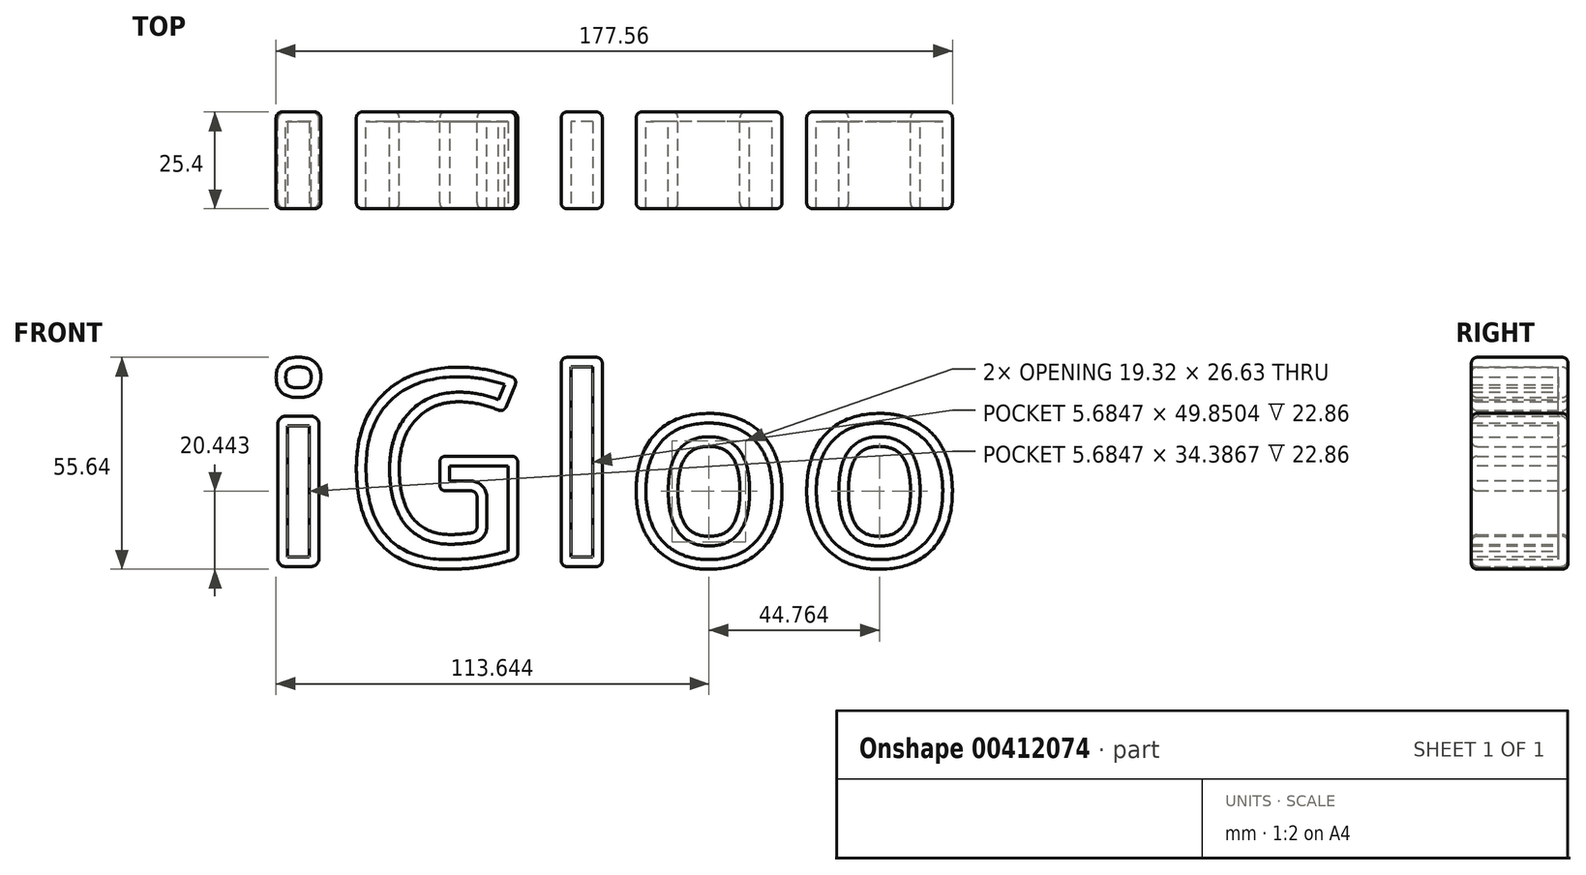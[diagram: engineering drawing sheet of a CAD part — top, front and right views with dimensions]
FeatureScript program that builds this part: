
annotation { "Feature Type Name" : "Feature", "Feature Type Description" : "" }
export const myFeature = defineFeature(function(context is Context, id is Id, definition is map)
    precondition{}
    {
        {
            var Q0;
            Q0=qCreatedBy(makeId("Front.planeOp"),FACE);
            var sketch = newSketch(context, id + "F0", { "sketchPlane" : qUnion([Q0])});
            skText(sketch, "E0", { "text": "iGloo", "fontName": "OpenSans-Bold.ttf"});
            const initialGuessF0  = {"E0": [-0.10189, -0.01132, 1, 0, 0.05205]};
            skSetInitialGuess(sketch, initialGuessF0);
            skSolve(sketch);
        }
        {
            var Q0;
            Q0 = qSketchRegion(id + "F0", true);
            var Q1;
            Q1 = qConstructionFilter(qBodyType(qCreatedBy(id + "F0" ,EDGE), BodyType.WIRE), ConstructionObject.NO);
            extrude(context, id + "F1", {"entities" : qUnion([Q0]), "surfaceEntities" : qUnion([Q1]), "depth" : 25.4 * mm});
        }
        {
            assignVariable(context, id + "F2", {"name" : "FilletAmount", "anyValue" : 1.52 * mm});
        }
        {
            var Q0;
            Q0=makeQuery(id+"F1.opExtrude","CAP_EDGE",EDGE,{"disambiguationData":[OSD([sQuery(id+"F0.wireOp",EDGE,"E0.sketch_text.stroke-7")])],"isStart":false});
            var Q1;
            Q1=makeQuery(id+"F1.opExtrude","CAP_EDGE",EDGE,{"disambiguationData":[OSD([sQuery(id+"F0.wireOp",EDGE,"E0.sketch_text.stroke-8")])],"isStart":false});
            var Q2;
            Q2=makeQuery(id+"F1.opExtrude","CAP_EDGE",EDGE,{"disambiguationData":[OSD([sQuery(id+"F0.wireOp",EDGE,"E0.sketch_text.stroke-6")])],"isStart":false});
            var Q3;
            Q3=makeQuery(id+"F1.opExtrude","CAP_EDGE",EDGE,{"disambiguationData":[OSD([sQuery(id+"F0.wireOp",EDGE,"E0.sketch_text.stroke-5")])],"isStart":false});
            var Q4;
            Q4=makeQuery(id+"F1.opExtrude","SWEPT_EDGE",EDGE,{"disambiguationData":[OSD([sQuery(id+"F0.wireOp",EDGE,"E0.sketch_text.stroke-7"),sQuery(id+"F0.wireOp",EDGE,"E0.sketch_text.stroke-8")])]});
            var Q5;
            Q5=makeQuery(id+"F1.opExtrude","CAP_EDGE",EDGE,{"disambiguationData":[OSD([sQuery(id+"F0.wireOp",EDGE,"E0.sketch_text.stroke-5")])],"isStart":true});
            var Q6;
            Q6=makeQuery(id+"F1.opExtrude","CAP_EDGE",EDGE,{"disambiguationData":[OSD([sQuery(id+"F0.wireOp",EDGE,"E0.sketch_text.stroke-7")])],"isStart":true});
            var Q7;
            Q7=makeQuery(id+"F1.opExtrude","SWEPT_EDGE",EDGE,{"disambiguationData":[OSD([sQuery(id+"F0.wireOp",EDGE,"E0.sketch_text.stroke-5"),sQuery(id+"F0.wireOp",EDGE,"E0.sketch_text.stroke-6")])]});
            var Q8;
            Q8=makeQuery(id+"F1.opExtrude","SWEPT_EDGE",EDGE,{"disambiguationData":[OSD([sQuery(id+"F0.wireOp",EDGE,"E0.sketch_text.stroke-6"),sQuery(id+"F0.wireOp",EDGE,"E0.sketch_text.stroke-7")])]});
            var Q9;
            Q9=makeQuery(id+"F1.opExtrude","SWEPT_EDGE",EDGE,{"disambiguationData":[OSD([sQuery(id+"F0.wireOp",EDGE,"E0.sketch_text.stroke-5"),sQuery(id+"F0.wireOp",EDGE,"E0.sketch_text.stroke-8")])]});
            var Q10;
            Q10=makeQuery(id+"F1.opExtrude","CAP_EDGE",EDGE,{"disambiguationData":[OSD([sQuery(id+"F0.wireOp",EDGE,"E0.sketch_text.stroke-6")])],"isStart":true});
            var Q11;
            Q11=makeQuery(id+"F1.opExtrude","CAP_EDGE",EDGE,{"disambiguationData":[OSD([sQuery(id+"F0.wireOp",EDGE,"E0.sketch_text.stroke-8")])],"isStart":true});
            fillet(context, id + "F3", {"entities" : qUnion([Q0, Q1, Q2, Q3, Q4, Q5, Q6, Q7, Q8, Q9, Q10, Q11]), "radius" : 2.03 * mm, "tangentPropagation" : true, "allowEdgeOverflow" : false});
        }
        {
            var Q0;
            Q0=makeQuery(id+"F1.opExtrude","SWEPT_FACE",FACE,{"disambiguationData":[OSD([sQuery(id+"F0.wireOp",EDGE,"E0.sketch_text.stroke-0")])]});
            var Q1;
            Q1=makeQuery(id+"F1.opExtrude","CAP_FACE",FACE,{"disambiguationData":[OSD([sQuery(id+"F0.wireOp",EDGE,"E0.sketch_text.stroke-0"),sQuery(id+"F0.wireOp",EDGE,"E0.sketch_text.stroke-1"),sQuery(id+"F0.wireOp",EDGE,"E0.sketch_text.stroke-2"),sQuery(id+"F0.wireOp",EDGE,"E0.sketch_text.stroke-3"),sQuery(id+"F0.wireOp",EDGE,"E0.sketch_text.stroke-4")])],"isStart":false});
            var Q2;
            Q2=makeQuery(id+"F1.opExtrude","SWEPT_FACE",FACE,{"disambiguationData":[OSD([sQuery(id+"F0.wireOp",EDGE,"E0.sketch_text.stroke-1")])]});
            var Q3;
            Q3=makeQuery(id+"F1.opExtrude","SWEPT_FACE",FACE,{"disambiguationData":[OSD([sQuery(id+"F0.wireOp",EDGE,"E0.sketch_text.stroke-2")])]});
            var Q4;
            Q4=makeQuery(id+"F1.opExtrude","SWEPT_FACE",FACE,{"disambiguationData":[OSD([sQuery(id+"F0.wireOp",EDGE,"E0.sketch_text.stroke-3")])]});
            var Q5;
            Q5=makeQuery(id+"F1.opExtrude","SWEPT_FACE",FACE,{"disambiguationData":[OSD([sQuery(id+"F0.wireOp",EDGE,"E0.sketch_text.stroke-4")])]});
            var Q6;
            Q6=makeQuery(id+"F1.opExtrude","CAP_EDGE",EDGE,{"disambiguationData":[OSD([sQuery(id+"F0.wireOp",EDGE,"E0.sketch_text.stroke-0")])],"isStart":false});
            var Q7;
            Q7=makeQuery(id+"F1.opExtrude","CAP_EDGE",EDGE,{"disambiguationData":[OSD([sQuery(id+"F0.wireOp",EDGE,"E0.sketch_text.stroke-1")])],"isStart":false});
            var Q8;
            Q8=makeQuery(id+"F1.opExtrude","SWEPT_EDGE",EDGE,{"disambiguationData":[OSD([sQuery(id+"F0.wireOp",EDGE,"E0.sketch_text.stroke-0"),sQuery(id+"F0.wireOp",EDGE,"E0.sketch_text.stroke-4")])]});
            var Q9;
            Q9=makeQuery(id+"F1.opExtrude","SWEPT_EDGE",EDGE,{"disambiguationData":[OSD([sQuery(id+"F0.wireOp",EDGE,"E0.sketch_text.stroke-0"),sQuery(id+"F0.wireOp",EDGE,"E0.sketch_text.stroke-1")])]});
            var Q10;
            Q10=makeQuery(id+"F1.opExtrude","CAP_FACE",FACE,{"disambiguationData":[OSD([sQuery(id+"F0.wireOp",EDGE,"E0.sketch_text.stroke-0"),sQuery(id+"F0.wireOp",EDGE,"E0.sketch_text.stroke-1"),sQuery(id+"F0.wireOp",EDGE,"E0.sketch_text.stroke-2"),sQuery(id+"F0.wireOp",EDGE,"E0.sketch_text.stroke-3"),sQuery(id+"F0.wireOp",EDGE,"E0.sketch_text.stroke-4")])],"isStart":true});
            var Q11;
            Q11=makeQuery(id+"F1.opExtrude","SWEPT_EDGE",EDGE,{"disambiguationData":[OSD([sQuery(id+"F0.wireOp",EDGE,"E0.sketch_text.stroke-1"),sQuery(id+"F0.wireOp",EDGE,"E0.sketch_text.stroke-2")])]});
            var Q12;
            Q12=makeQuery(id+"F1.opExtrude","SWEPT_EDGE",EDGE,{"disambiguationData":[OSD([sQuery(id+"F0.wireOp",EDGE,"E0.sketch_text.stroke-2"),sQuery(id+"F0.wireOp",EDGE,"E0.sketch_text.stroke-3")])]});
            var Q13;
            Q13=makeQuery(id+"F1.opExtrude","SWEPT_EDGE",EDGE,{"disambiguationData":[OSD([sQuery(id+"F0.wireOp",EDGE,"E0.sketch_text.stroke-3"),sQuery(id+"F0.wireOp",EDGE,"E0.sketch_text.stroke-4")])]});
            var Q14;
            Q14=makeQuery(id+"F1.opExtrude","CAP_EDGE",EDGE,{"disambiguationData":[OSD([sQuery(id+"F0.wireOp",EDGE,"E0.sketch_text.stroke-4")])],"isStart":false});
            var Q15;
            Q15=makeQuery(id+"F1.opExtrude","CAP_EDGE",EDGE,{"disambiguationData":[OSD([sQuery(id+"F0.wireOp",EDGE,"E0.sketch_text.stroke-0")])],"isStart":true});
            var Q16;
            Q16=makeQuery(id+"F1.opExtrude","CAP_EDGE",EDGE,{"disambiguationData":[OSD([sQuery(id+"F0.wireOp",EDGE,"E0.sketch_text.stroke-1")])],"isStart":true});
            var Q17;
            Q17=makeQuery(id+"F1.opExtrude","CAP_EDGE",EDGE,{"disambiguationData":[OSD([sQuery(id+"F0.wireOp",EDGE,"E0.sketch_text.stroke-2")])],"isStart":false});
            var Q18;
            Q18=makeQuery(id+"F1.opExtrude","CAP_EDGE",EDGE,{"disambiguationData":[OSD([sQuery(id+"F0.wireOp",EDGE,"E0.sketch_text.stroke-3")])],"isStart":false});
            var Q19;
            Q19=makeQuery(id+"F1.opExtrude","CAP_EDGE",EDGE,{"disambiguationData":[OSD([sQuery(id+"F0.wireOp",EDGE,"E0.sketch_text.stroke-2")])],"isStart":true});
            var Q20;
            Q20=makeQuery(id+"F1.opExtrude","CAP_EDGE",EDGE,{"disambiguationData":[OSD([sQuery(id+"F0.wireOp",EDGE,"E0.sketch_text.stroke-3")])],"isStart":true});
            var Q21;
            Q21=makeQuery(id+"F1.opExtrude","CAP_EDGE",EDGE,{"disambiguationData":[OSD([sQuery(id+"F0.wireOp",EDGE,"E0.sketch_text.stroke-4")])],"isStart":true});
            fillet(context, id + "F4", {"entities" : qUnion([Q0, Q1, Q2, Q3, Q4, Q5, Q6, Q7, Q8, Q9, Q10, Q11, Q12, Q13, Q14, Q15, Q16, Q17, Q18, Q19, Q20, Q21]), "radius" : getVariable(context, 'FilletAmount'), "tangentPropagation" : true, "allowEdgeOverflow" : false});
        }
        {
            var Q0;
            Q0=makeQuery(id+"F1.opExtrude","CAP_FACE",FACE,{"disambiguationData":[OSD([sQuery(id+"F0.wireOp",EDGE,"E0.sketch_text.stroke-9"),sQuery(id+"F0.wireOp",EDGE,"E0.sketch_text.stroke-10"),sQuery(id+"F0.wireOp",EDGE,"E0.sketch_text.stroke-11"),sQuery(id+"F0.wireOp",EDGE,"E0.sketch_text.stroke-12"),sQuery(id+"F0.wireOp",EDGE,"E0.sketch_text.stroke-13"),sQuery(id+"F0.wireOp",EDGE,"E0.sketch_text.stroke-14"),sQuery(id+"F0.wireOp",EDGE,"E0.sketch_text.stroke-15"),sQuery(id+"F0.wireOp",EDGE,"E0.sketch_text.stroke-16"),sQuery(id+"F0.wireOp",EDGE,"E0.sketch_text.stroke-17"),sQuery(id+"F0.wireOp",EDGE,"E0.sketch_text.stroke-18"),sQuery(id+"F0.wireOp",EDGE,"E0.sketch_text.stroke-19"),sQuery(id+"F0.wireOp",EDGE,"E0.sketch_text.stroke-20"),sQuery(id+"F0.wireOp",EDGE,"E0.sketch_text.stroke-21"),sQuery(id+"F0.wireOp",EDGE,"E0.sketch_text.stroke-22"),sQuery(id+"F0.wireOp",EDGE,"E0.sketch_text.stroke-23"),sQuery(id+"F0.wireOp",EDGE,"E0.sketch_text.stroke-24"),sQuery(id+"F0.wireOp",EDGE,"E0.sketch_text.stroke-25"),sQuery(id+"F0.wireOp",EDGE,"E0.sketch_text.stroke-26"),sQuery(id+"F0.wireOp",EDGE,"E0.sketch_text.stroke-27")])],"isStart":false});
            var Q1;
            Q1=makeQuery(id+"F1.opExtrude","SWEPT_FACE",FACE,{"disambiguationData":[OSD([sQuery(id+"F0.wireOp",EDGE,"E0.sketch_text.stroke-9")])]});
            var Q2;
            Q2=makeQuery(id+"F1.opExtrude","SWEPT_FACE",FACE,{"disambiguationData":[OSD([sQuery(id+"F0.wireOp",EDGE,"E0.sketch_text.stroke-25")])]});
            var Q3;
            Q3=makeQuery(id+"F1.opExtrude","CAP_EDGE",EDGE,{"disambiguationData":[OSD([sQuery(id+"F0.wireOp",EDGE,"E0.sketch_text.stroke-12")])],"isStart":false});
            var Q4;
            Q4=makeQuery(id+"F1.opExtrude","CAP_EDGE",EDGE,{"disambiguationData":[OSD([sQuery(id+"F0.wireOp",EDGE,"E0.sketch_text.stroke-20")])],"isStart":false});
            var Q5;
            Q5=makeQuery(id+"F1.opExtrude","SWEPT_FACE",FACE,{"disambiguationData":[OSD([sQuery(id+"F0.wireOp",EDGE,"E0.sketch_text.stroke-23")])]});
            var Q6;
            Q6=makeQuery(id+"F1.opExtrude","SWEPT_FACE",FACE,{"disambiguationData":[OSD([sQuery(id+"F0.wireOp",EDGE,"E0.sketch_text.stroke-24")])]});
            var Q7;
            Q7=makeQuery(id+"F1.opExtrude","CAP_EDGE",EDGE,{"disambiguationData":[OSD([sQuery(id+"F0.wireOp",EDGE,"E0.sketch_text.stroke-13")])],"isStart":false});
            var Q8;
            Q8=makeQuery(id+"F1.opExtrude","CAP_EDGE",EDGE,{"disambiguationData":[OSD([sQuery(id+"F0.wireOp",EDGE,"E0.sketch_text.stroke-21")])],"isStart":false});
            var Q9;
            Q9=makeQuery(id+"F1.opExtrude","SWEPT_FACE",FACE,{"disambiguationData":[OSD([sQuery(id+"F0.wireOp",EDGE,"E0.sketch_text.stroke-10")])]});
            var Q10;
            Q10=makeQuery(id+"F1.opExtrude","SWEPT_FACE",FACE,{"disambiguationData":[OSD([sQuery(id+"F0.wireOp",EDGE,"E0.sketch_text.stroke-26")])]});
            var Q11;
            Q11=makeQuery(id+"F1.opExtrude","CAP_EDGE",EDGE,{"disambiguationData":[OSD([sQuery(id+"F0.wireOp",EDGE,"E0.sketch_text.stroke-14")])],"isStart":false});
            var Q12;
            Q12=makeQuery(id+"F1.opExtrude","CAP_EDGE",EDGE,{"disambiguationData":[OSD([sQuery(id+"F0.wireOp",EDGE,"E0.sketch_text.stroke-22")])],"isStart":false});
            var Q13;
            Q13=makeQuery(id+"F1.opExtrude","CAP_EDGE",EDGE,{"disambiguationData":[OSD([sQuery(id+"F0.wireOp",EDGE,"E0.sketch_text.stroke-15")])],"isStart":false});
            var Q14;
            Q14=makeQuery(id+"F1.opExtrude","CAP_EDGE",EDGE,{"disambiguationData":[OSD([sQuery(id+"F0.wireOp",EDGE,"E0.sketch_text.stroke-23")])],"isStart":false});
            var Q15;
            Q15=makeQuery(id+"F1.opExtrude","SWEPT_FACE",FACE,{"disambiguationData":[OSD([sQuery(id+"F0.wireOp",EDGE,"E0.sketch_text.stroke-13")])]});
            var Q16;
            Q16=makeQuery(id+"F1.opExtrude","SWEPT_FACE",FACE,{"disambiguationData":[OSD([sQuery(id+"F0.wireOp",EDGE,"E0.sketch_text.stroke-14")])]});
            var Q17;
            Q17=makeQuery(id+"F1.opExtrude","CAP_EDGE",EDGE,{"disambiguationData":[OSD([sQuery(id+"F0.wireOp",EDGE,"E0.sketch_text.stroke-16")])],"isStart":false});
            var Q18;
            Q18=makeQuery(id+"F1.opExtrude","CAP_EDGE",EDGE,{"disambiguationData":[OSD([sQuery(id+"F0.wireOp",EDGE,"E0.sketch_text.stroke-24")])],"isStart":false});
            var Q19;
            Q19=makeQuery(id+"F1.opExtrude","SWEPT_FACE",FACE,{"disambiguationData":[OSD([sQuery(id+"F0.wireOp",EDGE,"E0.sketch_text.stroke-15")])]});
            var Q20;
            Q20=makeQuery(id+"F1.opExtrude","SWEPT_FACE",FACE,{"disambiguationData":[OSD([sQuery(id+"F0.wireOp",EDGE,"E0.sketch_text.stroke-16")])]});
            var Q21;
            Q21=makeQuery(id+"F1.opExtrude","CAP_EDGE",EDGE,{"disambiguationData":[OSD([sQuery(id+"F0.wireOp",EDGE,"E0.sketch_text.stroke-17")])],"isStart":false});
            var Q22;
            Q22=makeQuery(id+"F1.opExtrude","SWEPT_FACE",FACE,{"disambiguationData":[OSD([sQuery(id+"F0.wireOp",EDGE,"E0.sketch_text.stroke-17")])]});
            var Q23;
            Q23=makeQuery(id+"F1.opExtrude","CAP_EDGE",EDGE,{"disambiguationData":[OSD([sQuery(id+"F0.wireOp",EDGE,"E0.sketch_text.stroke-18")])],"isStart":false});
            var Q24;
            Q24=makeQuery(id+"F1.opExtrude","SWEPT_FACE",FACE,{"disambiguationData":[OSD([sQuery(id+"F0.wireOp",EDGE,"E0.sketch_text.stroke-19")])]});
            var Q25;
            Q25=makeQuery(id+"F1.opExtrude","SWEPT_FACE",FACE,{"disambiguationData":[OSD([sQuery(id+"F0.wireOp",EDGE,"E0.sketch_text.stroke-20")])]});
            var Q26;
            Q26=makeQuery(id+"F1.opExtrude","CAP_EDGE",EDGE,{"disambiguationData":[OSD([sQuery(id+"F0.wireOp",EDGE,"E0.sketch_text.stroke-11")])],"isStart":false});
            var Q27;
            Q27=makeQuery(id+"F1.opExtrude","CAP_EDGE",EDGE,{"disambiguationData":[OSD([sQuery(id+"F0.wireOp",EDGE,"E0.sketch_text.stroke-19")])],"isStart":false});
            var Q28;
            Q28=makeQuery(id+"F1.opExtrude","SWEPT_FACE",FACE,{"disambiguationData":[OSD([sQuery(id+"F0.wireOp",EDGE,"E0.sketch_text.stroke-21")])]});
            var Q29;
            Q29=makeQuery(id+"F1.opExtrude","SWEPT_FACE",FACE,{"disambiguationData":[OSD([sQuery(id+"F0.wireOp",EDGE,"E0.sketch_text.stroke-22")])]});
            var Q30;
            Q30=makeQuery(id+"F1.opExtrude","SWEPT_EDGE",EDGE,{"disambiguationData":[OSD([sQuery(id+"F0.wireOp",EDGE,"E0.sketch_text.stroke-13"),sQuery(id+"F0.wireOp",EDGE,"E0.sketch_text.stroke-14")])]});
            var Q31;
            Q31=makeQuery(id+"F1.opExtrude","CAP_FACE",FACE,{"disambiguationData":[OSD([sQuery(id+"F0.wireOp",EDGE,"E0.sketch_text.stroke-9"),sQuery(id+"F0.wireOp",EDGE,"E0.sketch_text.stroke-10"),sQuery(id+"F0.wireOp",EDGE,"E0.sketch_text.stroke-11"),sQuery(id+"F0.wireOp",EDGE,"E0.sketch_text.stroke-12"),sQuery(id+"F0.wireOp",EDGE,"E0.sketch_text.stroke-13"),sQuery(id+"F0.wireOp",EDGE,"E0.sketch_text.stroke-14"),sQuery(id+"F0.wireOp",EDGE,"E0.sketch_text.stroke-15"),sQuery(id+"F0.wireOp",EDGE,"E0.sketch_text.stroke-16"),sQuery(id+"F0.wireOp",EDGE,"E0.sketch_text.stroke-17"),sQuery(id+"F0.wireOp",EDGE,"E0.sketch_text.stroke-18"),sQuery(id+"F0.wireOp",EDGE,"E0.sketch_text.stroke-19"),sQuery(id+"F0.wireOp",EDGE,"E0.sketch_text.stroke-20"),sQuery(id+"F0.wireOp",EDGE,"E0.sketch_text.stroke-21"),sQuery(id+"F0.wireOp",EDGE,"E0.sketch_text.stroke-22"),sQuery(id+"F0.wireOp",EDGE,"E0.sketch_text.stroke-23"),sQuery(id+"F0.wireOp",EDGE,"E0.sketch_text.stroke-24"),sQuery(id+"F0.wireOp",EDGE,"E0.sketch_text.stroke-25"),sQuery(id+"F0.wireOp",EDGE,"E0.sketch_text.stroke-26"),sQuery(id+"F0.wireOp",EDGE,"E0.sketch_text.stroke-27")])],"isStart":true});
            var Q32;
            Q32=makeQuery(id+"F1.opExtrude","SWEPT_EDGE",EDGE,{"disambiguationData":[OSD([sQuery(id+"F0.wireOp",EDGE,"E0.sketch_text.stroke-14"),sQuery(id+"F0.wireOp",EDGE,"E0.sketch_text.stroke-15")])]});
            var Q33;
            Q33=makeQuery(id+"F1.opExtrude","SWEPT_EDGE",EDGE,{"disambiguationData":[OSD([sQuery(id+"F0.wireOp",EDGE,"E0.sketch_text.stroke-9"),sQuery(id+"F0.wireOp",EDGE,"E0.sketch_text.stroke-10")])]});
            var Q34;
            Q34=makeQuery(id+"F1.opExtrude","CAP_EDGE",EDGE,{"disambiguationData":[OSD([sQuery(id+"F0.wireOp",EDGE,"E0.sketch_text.stroke-13")])],"isStart":true});
            var Q35;
            Q35=makeQuery(id+"F1.opExtrude","CAP_EDGE",EDGE,{"disambiguationData":[OSD([sQuery(id+"F0.wireOp",EDGE,"E0.sketch_text.stroke-21")])],"isStart":true});
            var Q36;
            Q36=makeQuery(id+"F1.opExtrude","SWEPT_EDGE",EDGE,{"disambiguationData":[OSD([sQuery(id+"F0.wireOp",EDGE,"E0.sketch_text.stroke-15"),sQuery(id+"F0.wireOp",EDGE,"E0.sketch_text.stroke-16")])]});
            var Q37;
            Q37=makeQuery(id+"F1.opExtrude","CAP_EDGE",EDGE,{"disambiguationData":[OSD([sQuery(id+"F0.wireOp",EDGE,"E0.sketch_text.stroke-14")])],"isStart":true});
            var Q38;
            Q38=makeQuery(id+"F1.opExtrude","CAP_EDGE",EDGE,{"disambiguationData":[OSD([sQuery(id+"F0.wireOp",EDGE,"E0.sketch_text.stroke-22")])],"isStart":true});
            var Q39;
            Q39=makeQuery(id+"F1.opExtrude","SWEPT_EDGE",EDGE,{"disambiguationData":[OSD([sQuery(id+"F0.wireOp",EDGE,"E0.sketch_text.stroke-16"),sQuery(id+"F0.wireOp",EDGE,"E0.sketch_text.stroke-17")])]});
            var Q40;
            Q40=makeQuery(id+"F1.opExtrude","SWEPT_FACE",FACE,{"disambiguationData":[OSD([sQuery(id+"F0.wireOp",EDGE,"E0.sketch_text.stroke-11")])]});
            var Q41;
            Q41=makeQuery(id+"F1.opExtrude","SWEPT_FACE",FACE,{"disambiguationData":[OSD([sQuery(id+"F0.wireOp",EDGE,"E0.sketch_text.stroke-27")])]});
            var Q42;
            Q42=makeQuery(id+"F1.opExtrude","CAP_EDGE",EDGE,{"disambiguationData":[OSD([sQuery(id+"F0.wireOp",EDGE,"E0.sketch_text.stroke-15")])],"isStart":true});
            var Q43;
            Q43=makeQuery(id+"F1.opExtrude","CAP_EDGE",EDGE,{"disambiguationData":[OSD([sQuery(id+"F0.wireOp",EDGE,"E0.sketch_text.stroke-23")])],"isStart":true});
            var Q44;
            Q44=makeQuery(id+"F1.opExtrude","SWEPT_FACE",FACE,{"disambiguationData":[OSD([sQuery(id+"F0.wireOp",EDGE,"E0.sketch_text.stroke-12")])]});
            var Q45;
            Q45=makeQuery(id+"F1.opExtrude","SWEPT_EDGE",EDGE,{"disambiguationData":[OSD([sQuery(id+"F0.wireOp",EDGE,"E0.sketch_text.stroke-19"),sQuery(id+"F0.wireOp",EDGE,"E0.sketch_text.stroke-20")])]});
            var Q46;
            Q46=makeQuery(id+"F1.opExtrude","CAP_EDGE",EDGE,{"disambiguationData":[OSD([sQuery(id+"F0.wireOp",EDGE,"E0.sketch_text.stroke-16")])],"isStart":true});
            var Q47;
            Q47=makeQuery(id+"F1.opExtrude","CAP_EDGE",EDGE,{"disambiguationData":[OSD([sQuery(id+"F0.wireOp",EDGE,"E0.sketch_text.stroke-24")])],"isStart":true});
            var Q48;
            Q48=makeQuery(id+"F1.opExtrude","SWEPT_EDGE",EDGE,{"disambiguationData":[OSD([sQuery(id+"F0.wireOp",EDGE,"E0.sketch_text.stroke-20"),sQuery(id+"F0.wireOp",EDGE,"E0.sketch_text.stroke-21")])]});
            var Q49;
            Q49=makeQuery(id+"F1.opExtrude","SWEPT_EDGE",EDGE,{"disambiguationData":[OSD([sQuery(id+"F0.wireOp",EDGE,"E0.sketch_text.stroke-21"),sQuery(id+"F0.wireOp",EDGE,"E0.sketch_text.stroke-22")])]});
            var Q50;
            Q50=makeQuery(id+"F1.opExtrude","CAP_EDGE",EDGE,{"disambiguationData":[OSD([sQuery(id+"F0.wireOp",EDGE,"E0.sketch_text.stroke-17")])],"isStart":true});
            var Q51;
            Q51=makeQuery(id+"F1.opExtrude","SWEPT_EDGE",EDGE,{"disambiguationData":[OSD([sQuery(id+"F0.wireOp",EDGE,"E0.sketch_text.stroke-22"),sQuery(id+"F0.wireOp",EDGE,"E0.sketch_text.stroke-23")])]});
            var Q52;
            Q52=makeQuery(id+"F1.opExtrude","CAP_EDGE",EDGE,{"disambiguationData":[OSD([sQuery(id+"F0.wireOp",EDGE,"E0.sketch_text.stroke-9")])],"isStart":false});
            var Q53;
            Q53=makeQuery(id+"F1.opExtrude","CAP_EDGE",EDGE,{"disambiguationData":[OSD([sQuery(id+"F0.wireOp",EDGE,"E0.sketch_text.stroke-25")])],"isStart":false});
            var Q54;
            Q54=makeQuery(id+"F1.opExtrude","SWEPT_EDGE",EDGE,{"disambiguationData":[OSD([sQuery(id+"F0.wireOp",EDGE,"E0.sketch_text.stroke-23"),sQuery(id+"F0.wireOp",EDGE,"E0.sketch_text.stroke-24")])]});
            var Q55;
            Q55=makeQuery(id+"F1.opExtrude","CAP_EDGE",EDGE,{"disambiguationData":[OSD([sQuery(id+"F0.wireOp",EDGE,"E0.sketch_text.stroke-18")])],"isStart":true});
            var Q56;
            Q56=makeQuery(id+"F1.opExtrude","SWEPT_FACE",FACE,{"disambiguationData":[OSD([sQuery(id+"F0.wireOp",EDGE,"E0.sketch_text.stroke-18")])]});
            var Q57;
            Q57=makeQuery(id+"F1.opExtrude","CAP_EDGE",EDGE,{"disambiguationData":[OSD([sQuery(id+"F0.wireOp",EDGE,"E0.sketch_text.stroke-10")])],"isStart":false});
            var Q58;
            Q58=makeQuery(id+"F1.opExtrude","CAP_EDGE",EDGE,{"disambiguationData":[OSD([sQuery(id+"F0.wireOp",EDGE,"E0.sketch_text.stroke-26")])],"isStart":false});
            var Q59;
            Q59=makeQuery(id+"F1.opExtrude","CAP_EDGE",EDGE,{"disambiguationData":[OSD([sQuery(id+"F0.wireOp",EDGE,"E0.sketch_text.stroke-11")])],"isStart":true});
            var Q60;
            Q60=makeQuery(id+"F1.opExtrude","CAP_EDGE",EDGE,{"disambiguationData":[OSD([sQuery(id+"F0.wireOp",EDGE,"E0.sketch_text.stroke-19")])],"isStart":true});
            var Q61;
            Q61=makeQuery(id+"F1.opExtrude","CAP_EDGE",EDGE,{"disambiguationData":[OSD([sQuery(id+"F0.wireOp",EDGE,"E0.sketch_text.stroke-20")])],"isStart":true});
            var Q62;
            Q62=makeQuery(id+"F1.opExtrude","SWEPT_EDGE",EDGE,{"disambiguationData":[OSD([sQuery(id+"F0.wireOp",EDGE,"E0.sketch_text.stroke-12"),sQuery(id+"F0.wireOp",EDGE,"E0.sketch_text.stroke-13")])]});
            var Q63;
            Q63=makeQuery(id+"F1.opExtrude","SWEPT_EDGE",EDGE,{"disambiguationData":[OSD([sQuery(id+"F0.wireOp",EDGE,"E0.sketch_text.stroke-9"),sQuery(id+"F0.wireOp",EDGE,"E0.sketch_text.stroke-27")])]});
            var Q64;
            Q64=makeQuery(id+"F1.opExtrude","SWEPT_EDGE",EDGE,{"disambiguationData":[OSD([sQuery(id+"F0.wireOp",EDGE,"E0.sketch_text.stroke-10"),sQuery(id+"F0.wireOp",EDGE,"E0.sketch_text.stroke-11")])]});
            var Q65;
            Q65=makeQuery(id+"F1.opExtrude","SWEPT_EDGE",EDGE,{"disambiguationData":[OSD([sQuery(id+"F0.wireOp",EDGE,"E0.sketch_text.stroke-11"),sQuery(id+"F0.wireOp",EDGE,"E0.sketch_text.stroke-12")])]});
            var Q66;
            Q66=makeQuery(id+"F1.opExtrude","SWEPT_EDGE",EDGE,{"disambiguationData":[OSD([sQuery(id+"F0.wireOp",EDGE,"E0.sketch_text.stroke-17"),sQuery(id+"F0.wireOp",EDGE,"E0.sketch_text.stroke-18")])]});
            var Q67;
            Q67=makeQuery(id+"F1.opExtrude","SWEPT_EDGE",EDGE,{"disambiguationData":[OSD([sQuery(id+"F0.wireOp",EDGE,"E0.sketch_text.stroke-18"),sQuery(id+"F0.wireOp",EDGE,"E0.sketch_text.stroke-19")])]});
            var Q68;
            Q68=makeQuery(id+"F1.opExtrude","CAP_EDGE",EDGE,{"disambiguationData":[OSD([sQuery(id+"F0.wireOp",EDGE,"E0.sketch_text.stroke-9")])],"isStart":true});
            var Q69;
            Q69=makeQuery(id+"F1.opExtrude","CAP_EDGE",EDGE,{"disambiguationData":[OSD([sQuery(id+"F0.wireOp",EDGE,"E0.sketch_text.stroke-25")])],"isStart":true});
            var Q70;
            Q70=makeQuery(id+"F1.opExtrude","CAP_EDGE",EDGE,{"disambiguationData":[OSD([sQuery(id+"F0.wireOp",EDGE,"E0.sketch_text.stroke-10")])],"isStart":true});
            var Q71;
            Q71=makeQuery(id+"F1.opExtrude","CAP_EDGE",EDGE,{"disambiguationData":[OSD([sQuery(id+"F0.wireOp",EDGE,"E0.sketch_text.stroke-26")])],"isStart":true});
            var Q72;
            Q72=makeQuery(id+"F1.opExtrude","SWEPT_EDGE",EDGE,{"disambiguationData":[OSD([sQuery(id+"F0.wireOp",EDGE,"E0.sketch_text.stroke-24"),sQuery(id+"F0.wireOp",EDGE,"E0.sketch_text.stroke-25")])]});
            var Q73;
            Q73=makeQuery(id+"F1.opExtrude","SWEPT_EDGE",EDGE,{"disambiguationData":[OSD([sQuery(id+"F0.wireOp",EDGE,"E0.sketch_text.stroke-25"),sQuery(id+"F0.wireOp",EDGE,"E0.sketch_text.stroke-26")])]});
            var Q74;
            Q74=makeQuery(id+"F1.opExtrude","SWEPT_EDGE",EDGE,{"disambiguationData":[OSD([sQuery(id+"F0.wireOp",EDGE,"E0.sketch_text.stroke-26"),sQuery(id+"F0.wireOp",EDGE,"E0.sketch_text.stroke-27")])]});
            var Q75;
            Q75=makeQuery(id+"F1.opExtrude","CAP_EDGE",EDGE,{"disambiguationData":[OSD([sQuery(id+"F0.wireOp",EDGE,"E0.sketch_text.stroke-27")])],"isStart":false});
            var Q76;
            Q76=makeQuery(id+"F1.opExtrude","CAP_EDGE",EDGE,{"disambiguationData":[OSD([sQuery(id+"F0.wireOp",EDGE,"E0.sketch_text.stroke-12")])],"isStart":true});
            var Q77;
            Q77=makeQuery(id+"F1.opExtrude","CAP_EDGE",EDGE,{"disambiguationData":[OSD([sQuery(id+"F0.wireOp",EDGE,"E0.sketch_text.stroke-27")])],"isStart":true});
            fillet(context, id + "F5", {"entities" : qUnion([Q0, Q1, Q2, Q3, Q4, Q5, Q6, Q7, Q8, Q9, Q10, Q11, Q12, Q13, Q14, Q15, Q16, Q17, Q18, Q19, Q20, Q21, Q22, Q23, Q24, Q25, Q26, Q27, Q28, Q29, Q30, Q31, Q32, Q33, Q34, Q35, Q36, Q37, Q38, Q39, Q40, Q41, Q42, Q43, Q44, Q45, Q46, Q47, Q48, Q49, Q50, Q51, Q52, Q53, Q54, Q55, Q56, Q57, Q58, Q59, Q60, Q61, Q62, Q63, Q64, Q65, Q66, Q67, Q68, Q69, Q70, Q71, Q72, Q73, Q74, Q75, Q76, Q77]), "radius" : getVariable(context, 'FilletAmount'), "tangentPropagation" : true, "allowEdgeOverflow" : false});
        }
        {
            var Q0;
            Q0=makeQuery(id+"F1.opExtrude","CAP_FACE",FACE,{"disambiguationData":[OSD([sQuery(id+"F0.wireOp",EDGE,"E0.sketch_text.stroke-28"),sQuery(id+"F0.wireOp",EDGE,"E0.sketch_text.stroke-29"),sQuery(id+"F0.wireOp",EDGE,"E0.sketch_text.stroke-30"),sQuery(id+"F0.wireOp",EDGE,"E0.sketch_text.stroke-31")])],"isStart":false});
            var Q1;
            Q1=makeQuery(id+"F1.opExtrude","SWEPT_EDGE",EDGE,{"disambiguationData":[OSD([sQuery(id+"F0.wireOp",EDGE,"E0.sketch_text.stroke-30"),sQuery(id+"F0.wireOp",EDGE,"E0.sketch_text.stroke-31")])]});
            var Q2;
            Q2=makeQuery(id+"F1.opExtrude","SWEPT_EDGE",EDGE,{"disambiguationData":[OSD([sQuery(id+"F0.wireOp",EDGE,"E0.sketch_text.stroke-28"),sQuery(id+"F0.wireOp",EDGE,"E0.sketch_text.stroke-29")])]});
            var Q3;
            Q3=makeQuery(id+"F1.opExtrude","SWEPT_EDGE",EDGE,{"disambiguationData":[OSD([sQuery(id+"F0.wireOp",EDGE,"E0.sketch_text.stroke-29"),sQuery(id+"F0.wireOp",EDGE,"E0.sketch_text.stroke-30")])]});
            var Q4;
            Q4=makeQuery(id+"F1.opExtrude","CAP_EDGE",EDGE,{"disambiguationData":[OSD([sQuery(id+"F0.wireOp",EDGE,"E0.sketch_text.stroke-30")])],"isStart":false});
            var Q5;
            Q5=makeQuery(id+"F1.opExtrude","CAP_EDGE",EDGE,{"disambiguationData":[OSD([sQuery(id+"F0.wireOp",EDGE,"E0.sketch_text.stroke-29")])],"isStart":true});
            var Q6;
            Q6=makeQuery(id+"F1.opExtrude","CAP_EDGE",EDGE,{"disambiguationData":[OSD([sQuery(id+"F0.wireOp",EDGE,"E0.sketch_text.stroke-30")])],"isStart":true});
            var Q7;
            Q7=makeQuery(id+"F1.opExtrude","CAP_EDGE",EDGE,{"disambiguationData":[OSD([sQuery(id+"F0.wireOp",EDGE,"E0.sketch_text.stroke-31")])],"isStart":true});
            var Q8;
            Q8=makeQuery(id+"F1.opExtrude","CAP_EDGE",EDGE,{"disambiguationData":[OSD([sQuery(id+"F0.wireOp",EDGE,"E0.sketch_text.stroke-28")])],"isStart":true});
            var Q9;
            Q9=makeQuery(id+"F1.opExtrude","CAP_EDGE",EDGE,{"disambiguationData":[OSD([sQuery(id+"F0.wireOp",EDGE,"E0.sketch_text.stroke-28")])],"isStart":false});
            var Q10;
            Q10=makeQuery(id+"F1.opExtrude","SWEPT_EDGE",EDGE,{"disambiguationData":[OSD([sQuery(id+"F0.wireOp",EDGE,"E0.sketch_text.stroke-28"),sQuery(id+"F0.wireOp",EDGE,"E0.sketch_text.stroke-31")])]});
            var Q11;
            Q11=makeQuery(id+"F1.opExtrude","CAP_EDGE",EDGE,{"disambiguationData":[OSD([sQuery(id+"F0.wireOp",EDGE,"E0.sketch_text.stroke-29")])],"isStart":false});
            var Q12;
            Q12=makeQuery(id+"F1.opExtrude","CAP_EDGE",EDGE,{"disambiguationData":[OSD([sQuery(id+"F0.wireOp",EDGE,"E0.sketch_text.stroke-31")])],"isStart":false});
            fillet(context, id + "F6", {"entities" : qUnion([Q0, Q1, Q2, Q3, Q4, Q5, Q6, Q7, Q8, Q9, Q10, Q11, Q12]), "radius" : getVariable(context, 'FilletAmount'), "tangentPropagation" : true, "allowEdgeOverflow" : false});
        }
        {
            var Q0;
            Q0=makeQuery(id+"F1.opExtrude","SWEPT_FACE",FACE,{"disambiguationData":[OSD([sQuery(id+"F0.wireOp",EDGE,"E0.sketch_text.stroke-37")])]});
            var Q1;
            Q1=makeQuery(id+"F1.opExtrude","CAP_EDGE",EDGE,{"disambiguationData":[OSD([sQuery(id+"F0.wireOp",EDGE,"E0.sketch_text.stroke-36")])],"isStart":false});
            var Q2;
            Q2=makeQuery(id+"F1.opExtrude","CAP_EDGE",EDGE,{"disambiguationData":[OSD([sQuery(id+"F0.wireOp",EDGE,"E0.sketch_text.stroke-44")])],"isStart":false});
            var Q3;
            Q3=makeQuery(id+"F1.opExtrude","SWEPT_FACE",FACE,{"disambiguationData":[OSD([sQuery(id+"F0.wireOp",EDGE,"E0.sketch_text.stroke-35")])]});
            var Q4;
            Q4=makeQuery(id+"F1.opExtrude","SWEPT_FACE",FACE,{"disambiguationData":[OSD([sQuery(id+"F0.wireOp",EDGE,"E0.sketch_text.stroke-36")])]});
            var Q5;
            Q5=makeQuery(id+"F1.opExtrude","CAP_EDGE",EDGE,{"disambiguationData":[OSD([sQuery(id+"F0.wireOp",EDGE,"E0.sketch_text.stroke-37")])],"isStart":false});
            var Q6;
            Q6=makeQuery(id+"F1.opExtrude","CAP_EDGE",EDGE,{"disambiguationData":[OSD([sQuery(id+"F0.wireOp",EDGE,"E0.sketch_text.stroke-45")])],"isStart":false});
            var Q7;
            Q7=makeQuery(id+"F1.opExtrude","SWEPT_FACE",FACE,{"disambiguationData":[OSD([sQuery(id+"F0.wireOp",EDGE,"E0.sketch_text.stroke-38")])]});
            var Q8;
            Q8=makeQuery(id+"F1.opExtrude","CAP_EDGE",EDGE,{"disambiguationData":[OSD([sQuery(id+"F0.wireOp",EDGE,"E0.sketch_text.stroke-38")])],"isStart":false});
            var Q9;
            Q9=makeQuery(id+"F1.opExtrude","CAP_EDGE",EDGE,{"disambiguationData":[OSD([sQuery(id+"F0.wireOp",EDGE,"E0.sketch_text.stroke-46")])],"isStart":false});
            var Q10;
            Q10=makeQuery(id+"F1.opExtrude","SWEPT_FACE",FACE,{"disambiguationData":[OSD([sQuery(id+"F0.wireOp",EDGE,"E0.sketch_text.stroke-39")])]});
            var Q11;
            Q11=makeQuery(id+"F1.opExtrude","SWEPT_FACE",FACE,{"disambiguationData":[OSD([sQuery(id+"F0.wireOp",EDGE,"E0.sketch_text.stroke-40")])]});
            var Q12;
            Q12=makeQuery(id+"F1.opExtrude","CAP_EDGE",EDGE,{"disambiguationData":[OSD([sQuery(id+"F0.wireOp",EDGE,"E0.sketch_text.stroke-39")])],"isStart":false});
            var Q13;
            Q13=makeQuery(id+"F1.opExtrude","CAP_EDGE",EDGE,{"disambiguationData":[OSD([sQuery(id+"F0.wireOp",EDGE,"E0.sketch_text.stroke-47")])],"isStart":false});
            var Q14;
            Q14=makeQuery(id+"F1.opExtrude","SWEPT_FACE",FACE,{"disambiguationData":[OSD([sQuery(id+"F0.wireOp",EDGE,"E0.sketch_text.stroke-41")])]});
            var Q15;
            Q15=makeQuery(id+"F1.opExtrude","SWEPT_FACE",FACE,{"disambiguationData":[OSD([sQuery(id+"F0.wireOp",EDGE,"E0.sketch_text.stroke-42")])]});
            var Q16;
            Q16=makeQuery(id+"F1.opExtrude","CAP_EDGE",EDGE,{"disambiguationData":[OSD([sQuery(id+"F0.wireOp",EDGE,"E0.sketch_text.stroke-32")])],"isStart":false});
            var Q17;
            Q17=makeQuery(id+"F1.opExtrude","CAP_EDGE",EDGE,{"disambiguationData":[OSD([sQuery(id+"F0.wireOp",EDGE,"E0.sketch_text.stroke-40")])],"isStart":false});
            var Q18;
            Q18=makeQuery(id+"F1.opExtrude","CAP_EDGE",EDGE,{"disambiguationData":[OSD([sQuery(id+"F0.wireOp",EDGE,"E0.sketch_text.stroke-48")])],"isStart":false});
            var Q19;
            Q19=makeQuery(id+"F1.opExtrude","SWEPT_FACE",FACE,{"disambiguationData":[OSD([sQuery(id+"F0.wireOp",EDGE,"E0.sketch_text.stroke-43")])]});
            var Q20;
            Q20=makeQuery(id+"F1.opExtrude","SWEPT_FACE",FACE,{"disambiguationData":[OSD([sQuery(id+"F0.wireOp",EDGE,"E0.sketch_text.stroke-44")])]});
            var Q21;
            Q21=makeQuery(id+"F1.opExtrude","CAP_EDGE",EDGE,{"disambiguationData":[OSD([sQuery(id+"F0.wireOp",EDGE,"E0.sketch_text.stroke-33")])],"isStart":false});
            var Q22;
            Q22=makeQuery(id+"F1.opExtrude","CAP_EDGE",EDGE,{"disambiguationData":[OSD([sQuery(id+"F0.wireOp",EDGE,"E0.sketch_text.stroke-41")])],"isStart":false});
            var Q23;
            Q23=makeQuery(id+"F1.opExtrude","CAP_EDGE",EDGE,{"disambiguationData":[OSD([sQuery(id+"F0.wireOp",EDGE,"E0.sketch_text.stroke-49")])],"isStart":false});
            var Q24;
            Q24=makeQuery(id+"F1.opExtrude","SWEPT_FACE",FACE,{"disambiguationData":[OSD([sQuery(id+"F0.wireOp",EDGE,"E0.sketch_text.stroke-45")])]});
            var Q25;
            Q25=makeQuery(id+"F1.opExtrude","SWEPT_FACE",FACE,{"disambiguationData":[OSD([sQuery(id+"F0.wireOp",EDGE,"E0.sketch_text.stroke-32")])]});
            var Q26;
            Q26=makeQuery(id+"F1.opExtrude","SWEPT_FACE",FACE,{"disambiguationData":[OSD([sQuery(id+"F0.wireOp",EDGE,"E0.sketch_text.stroke-46")])]});
            var Q27;
            Q27=makeQuery(id+"F1.opExtrude","CAP_EDGE",EDGE,{"disambiguationData":[OSD([sQuery(id+"F0.wireOp",EDGE,"E0.sketch_text.stroke-34")])],"isStart":false});
            var Q28;
            Q28=makeQuery(id+"F1.opExtrude","CAP_EDGE",EDGE,{"disambiguationData":[OSD([sQuery(id+"F0.wireOp",EDGE,"E0.sketch_text.stroke-42")])],"isStart":false});
            var Q29;
            Q29=makeQuery(id+"F1.opExtrude","SWEPT_FACE",FACE,{"disambiguationData":[OSD([sQuery(id+"F0.wireOp",EDGE,"E0.sketch_text.stroke-47")])]});
            var Q30;
            Q30=makeQuery(id+"F1.opExtrude","CAP_FACE",FACE,{"disambiguationData":[OSD([sQuery(id+"F0.wireOp",EDGE,"E0.sketch_text.stroke-32"),sQuery(id+"F0.wireOp",EDGE,"E0.sketch_text.stroke-33"),sQuery(id+"F0.wireOp",EDGE,"E0.sketch_text.stroke-34"),sQuery(id+"F0.wireOp",EDGE,"E0.sketch_text.stroke-35"),sQuery(id+"F0.wireOp",EDGE,"E0.sketch_text.stroke-36"),sQuery(id+"F0.wireOp",EDGE,"E0.sketch_text.stroke-37"),sQuery(id+"F0.wireOp",EDGE,"E0.sketch_text.stroke-38"),sQuery(id+"F0.wireOp",EDGE,"E0.sketch_text.stroke-39"),sQuery(id+"F0.wireOp",EDGE,"E0.sketch_text.stroke-40"),sQuery(id+"F0.wireOp",EDGE,"E0.sketch_text.stroke-41"),sQuery(id+"F0.wireOp",EDGE,"E0.sketch_text.stroke-42"),sQuery(id+"F0.wireOp",EDGE,"E0.sketch_text.stroke-43"),sQuery(id+"F0.wireOp",EDGE,"E0.sketch_text.stroke-44"),sQuery(id+"F0.wireOp",EDGE,"E0.sketch_text.stroke-45"),sQuery(id+"F0.wireOp",EDGE,"E0.sketch_text.stroke-46"),sQuery(id+"F0.wireOp",EDGE,"E0.sketch_text.stroke-47"),sQuery(id+"F0.wireOp",EDGE,"E0.sketch_text.stroke-48"),sQuery(id+"F0.wireOp",EDGE,"E0.sketch_text.stroke-49")])],"isStart":false});
            var Q31;
            Q31=makeQuery(id+"F1.opExtrude","SWEPT_FACE",FACE,{"disambiguationData":[OSD([sQuery(id+"F0.wireOp",EDGE,"E0.sketch_text.stroke-48")])]});
            var Q32;
            Q32=makeQuery(id+"F1.opExtrude","CAP_EDGE",EDGE,{"disambiguationData":[OSD([sQuery(id+"F0.wireOp",EDGE,"E0.sketch_text.stroke-35")])],"isStart":false});
            var Q33;
            Q33=makeQuery(id+"F1.opExtrude","CAP_EDGE",EDGE,{"disambiguationData":[OSD([sQuery(id+"F0.wireOp",EDGE,"E0.sketch_text.stroke-43")])],"isStart":false});
            var Q34;
            Q34=makeQuery(id+"F1.opExtrude","SWEPT_FACE",FACE,{"disambiguationData":[OSD([sQuery(id+"F0.wireOp",EDGE,"E0.sketch_text.stroke-33")])]});
            var Q35;
            Q35=makeQuery(id+"F1.opExtrude","SWEPT_FACE",FACE,{"disambiguationData":[OSD([sQuery(id+"F0.wireOp",EDGE,"E0.sketch_text.stroke-49")])]});
            var Q36;
            Q36=makeQuery(id+"F1.opExtrude","SWEPT_FACE",FACE,{"disambiguationData":[OSD([sQuery(id+"F0.wireOp",EDGE,"E0.sketch_text.stroke-34")])]});
            var Q37;
            Q37=makeQuery(id+"F1.opExtrude","SWEPT_EDGE",EDGE,{"disambiguationData":[OSD([sQuery(id+"F0.wireOp",EDGE,"E0.sketch_text.stroke-44"),sQuery(id+"F0.wireOp",EDGE,"E0.sketch_text.stroke-45")])]});
            var Q38;
            Q38=makeQuery(id+"F1.opExtrude","SWEPT_EDGE",EDGE,{"disambiguationData":[OSD([sQuery(id+"F0.wireOp",EDGE,"E0.sketch_text.stroke-45"),sQuery(id+"F0.wireOp",EDGE,"E0.sketch_text.stroke-46")])]});
            var Q39;
            Q39=makeQuery(id+"F1.opExtrude","CAP_EDGE",EDGE,{"disambiguationData":[OSD([sQuery(id+"F0.wireOp",EDGE,"E0.sketch_text.stroke-37")])],"isStart":true});
            var Q40;
            Q40=makeQuery(id+"F1.opExtrude","CAP_EDGE",EDGE,{"disambiguationData":[OSD([sQuery(id+"F0.wireOp",EDGE,"E0.sketch_text.stroke-45")])],"isStart":true});
            var Q41;
            Q41=makeQuery(id+"F1.opExtrude","SWEPT_EDGE",EDGE,{"disambiguationData":[OSD([sQuery(id+"F0.wireOp",EDGE,"E0.sketch_text.stroke-46"),sQuery(id+"F0.wireOp",EDGE,"E0.sketch_text.stroke-47")])]});
            var Q42;
            Q42=makeQuery(id+"F1.opExtrude","SWEPT_EDGE",EDGE,{"disambiguationData":[OSD([sQuery(id+"F0.wireOp",EDGE,"E0.sketch_text.stroke-32"),sQuery(id+"F0.wireOp",EDGE,"E0.sketch_text.stroke-39")])]});
            var Q43;
            Q43=makeQuery(id+"F1.opExtrude","SWEPT_EDGE",EDGE,{"disambiguationData":[OSD([sQuery(id+"F0.wireOp",EDGE,"E0.sketch_text.stroke-47"),sQuery(id+"F0.wireOp",EDGE,"E0.sketch_text.stroke-48")])]});
            var Q44;
            Q44=makeQuery(id+"F1.opExtrude","CAP_EDGE",EDGE,{"disambiguationData":[OSD([sQuery(id+"F0.wireOp",EDGE,"E0.sketch_text.stroke-38")])],"isStart":true});
            var Q45;
            Q45=makeQuery(id+"F1.opExtrude","CAP_EDGE",EDGE,{"disambiguationData":[OSD([sQuery(id+"F0.wireOp",EDGE,"E0.sketch_text.stroke-46")])],"isStart":true});
            var Q46;
            Q46=makeQuery(id+"F1.opExtrude","SWEPT_EDGE",EDGE,{"disambiguationData":[OSD([sQuery(id+"F0.wireOp",EDGE,"E0.sketch_text.stroke-32"),sQuery(id+"F0.wireOp",EDGE,"E0.sketch_text.stroke-33")])]});
            var Q47;
            Q47=makeQuery(id+"F1.opExtrude","SWEPT_EDGE",EDGE,{"disambiguationData":[OSD([sQuery(id+"F0.wireOp",EDGE,"E0.sketch_text.stroke-48"),sQuery(id+"F0.wireOp",EDGE,"E0.sketch_text.stroke-49")])]});
            var Q48;
            Q48=makeQuery(id+"F1.opExtrude","SWEPT_EDGE",EDGE,{"disambiguationData":[OSD([sQuery(id+"F0.wireOp",EDGE,"E0.sketch_text.stroke-33"),sQuery(id+"F0.wireOp",EDGE,"E0.sketch_text.stroke-34")])]});
            var Q49;
            Q49=makeQuery(id+"F1.opExtrude","CAP_EDGE",EDGE,{"disambiguationData":[OSD([sQuery(id+"F0.wireOp",EDGE,"E0.sketch_text.stroke-39")])],"isStart":true});
            var Q50;
            Q50=makeQuery(id+"F1.opExtrude","CAP_EDGE",EDGE,{"disambiguationData":[OSD([sQuery(id+"F0.wireOp",EDGE,"E0.sketch_text.stroke-47")])],"isStart":true});
            var Q51;
            Q51=makeQuery(id+"F1.opExtrude","SWEPT_EDGE",EDGE,{"disambiguationData":[OSD([sQuery(id+"F0.wireOp",EDGE,"E0.sketch_text.stroke-34"),sQuery(id+"F0.wireOp",EDGE,"E0.sketch_text.stroke-35")])]});
            var Q52;
            Q52=makeQuery(id+"F1.opExtrude","SWEPT_EDGE",EDGE,{"disambiguationData":[OSD([sQuery(id+"F0.wireOp",EDGE,"E0.sketch_text.stroke-35"),sQuery(id+"F0.wireOp",EDGE,"E0.sketch_text.stroke-36")])]});
            var Q53;
            Q53=makeQuery(id+"F1.opExtrude","CAP_EDGE",EDGE,{"disambiguationData":[OSD([sQuery(id+"F0.wireOp",EDGE,"E0.sketch_text.stroke-32")])],"isStart":true});
            var Q54;
            Q54=makeQuery(id+"F1.opExtrude","CAP_EDGE",EDGE,{"disambiguationData":[OSD([sQuery(id+"F0.wireOp",EDGE,"E0.sketch_text.stroke-40")])],"isStart":true});
            var Q55;
            Q55=makeQuery(id+"F1.opExtrude","CAP_EDGE",EDGE,{"disambiguationData":[OSD([sQuery(id+"F0.wireOp",EDGE,"E0.sketch_text.stroke-48")])],"isStart":true});
            var Q56;
            Q56=makeQuery(id+"F1.opExtrude","SWEPT_EDGE",EDGE,{"disambiguationData":[OSD([sQuery(id+"F0.wireOp",EDGE,"E0.sketch_text.stroke-36"),sQuery(id+"F0.wireOp",EDGE,"E0.sketch_text.stroke-37")])]});
            var Q57;
            Q57=makeQuery(id+"F1.opExtrude","SWEPT_EDGE",EDGE,{"disambiguationData":[OSD([sQuery(id+"F0.wireOp",EDGE,"E0.sketch_text.stroke-37"),sQuery(id+"F0.wireOp",EDGE,"E0.sketch_text.stroke-38")])]});
            var Q58;
            Q58=makeQuery(id+"F1.opExtrude","CAP_EDGE",EDGE,{"disambiguationData":[OSD([sQuery(id+"F0.wireOp",EDGE,"E0.sketch_text.stroke-33")])],"isStart":true});
            var Q59;
            Q59=makeQuery(id+"F1.opExtrude","CAP_EDGE",EDGE,{"disambiguationData":[OSD([sQuery(id+"F0.wireOp",EDGE,"E0.sketch_text.stroke-41")])],"isStart":true});
            var Q60;
            Q60=makeQuery(id+"F1.opExtrude","CAP_EDGE",EDGE,{"disambiguationData":[OSD([sQuery(id+"F0.wireOp",EDGE,"E0.sketch_text.stroke-49")])],"isStart":true});
            var Q61;
            Q61=makeQuery(id+"F1.opExtrude","SWEPT_EDGE",EDGE,{"disambiguationData":[OSD([sQuery(id+"F0.wireOp",EDGE,"E0.sketch_text.stroke-38"),sQuery(id+"F0.wireOp",EDGE,"E0.sketch_text.stroke-39")])]});
            var Q62;
            Q62=makeQuery(id+"F1.opExtrude","SWEPT_EDGE",EDGE,{"disambiguationData":[OSD([sQuery(id+"F0.wireOp",EDGE,"E0.sketch_text.stroke-40"),sQuery(id+"F0.wireOp",EDGE,"E0.sketch_text.stroke-49")])]});
            var Q63;
            Q63=makeQuery(id+"F1.opExtrude","CAP_EDGE",EDGE,{"disambiguationData":[OSD([sQuery(id+"F0.wireOp",EDGE,"E0.sketch_text.stroke-34")])],"isStart":true});
            var Q64;
            Q64=makeQuery(id+"F1.opExtrude","CAP_EDGE",EDGE,{"disambiguationData":[OSD([sQuery(id+"F0.wireOp",EDGE,"E0.sketch_text.stroke-42")])],"isStart":true});
            var Q65;
            Q65=makeQuery(id+"F1.opExtrude","SWEPT_EDGE",EDGE,{"disambiguationData":[OSD([sQuery(id+"F0.wireOp",EDGE,"E0.sketch_text.stroke-40"),sQuery(id+"F0.wireOp",EDGE,"E0.sketch_text.stroke-41")])]});
            var Q66;
            Q66=makeQuery(id+"F1.opExtrude","CAP_FACE",FACE,{"disambiguationData":[OSD([sQuery(id+"F0.wireOp",EDGE,"E0.sketch_text.stroke-32"),sQuery(id+"F0.wireOp",EDGE,"E0.sketch_text.stroke-33"),sQuery(id+"F0.wireOp",EDGE,"E0.sketch_text.stroke-34"),sQuery(id+"F0.wireOp",EDGE,"E0.sketch_text.stroke-35"),sQuery(id+"F0.wireOp",EDGE,"E0.sketch_text.stroke-36"),sQuery(id+"F0.wireOp",EDGE,"E0.sketch_text.stroke-37"),sQuery(id+"F0.wireOp",EDGE,"E0.sketch_text.stroke-38"),sQuery(id+"F0.wireOp",EDGE,"E0.sketch_text.stroke-39"),sQuery(id+"F0.wireOp",EDGE,"E0.sketch_text.stroke-40"),sQuery(id+"F0.wireOp",EDGE,"E0.sketch_text.stroke-41"),sQuery(id+"F0.wireOp",EDGE,"E0.sketch_text.stroke-42"),sQuery(id+"F0.wireOp",EDGE,"E0.sketch_text.stroke-43"),sQuery(id+"F0.wireOp",EDGE,"E0.sketch_text.stroke-44"),sQuery(id+"F0.wireOp",EDGE,"E0.sketch_text.stroke-45"),sQuery(id+"F0.wireOp",EDGE,"E0.sketch_text.stroke-46"),sQuery(id+"F0.wireOp",EDGE,"E0.sketch_text.stroke-47"),sQuery(id+"F0.wireOp",EDGE,"E0.sketch_text.stroke-48"),sQuery(id+"F0.wireOp",EDGE,"E0.sketch_text.stroke-49")])],"isStart":true});
            var Q67;
            Q67=makeQuery(id+"F1.opExtrude","SWEPT_EDGE",EDGE,{"disambiguationData":[OSD([sQuery(id+"F0.wireOp",EDGE,"E0.sketch_text.stroke-41"),sQuery(id+"F0.wireOp",EDGE,"E0.sketch_text.stroke-42")])]});
            var Q68;
            Q68=makeQuery(id+"F1.opExtrude","CAP_EDGE",EDGE,{"disambiguationData":[OSD([sQuery(id+"F0.wireOp",EDGE,"E0.sketch_text.stroke-35")])],"isStart":true});
            var Q69;
            Q69=makeQuery(id+"F1.opExtrude","CAP_EDGE",EDGE,{"disambiguationData":[OSD([sQuery(id+"F0.wireOp",EDGE,"E0.sketch_text.stroke-43")])],"isStart":true});
            var Q70;
            Q70=makeQuery(id+"F1.opExtrude","SWEPT_EDGE",EDGE,{"disambiguationData":[OSD([sQuery(id+"F0.wireOp",EDGE,"E0.sketch_text.stroke-42"),sQuery(id+"F0.wireOp",EDGE,"E0.sketch_text.stroke-43")])]});
            var Q71;
            Q71=makeQuery(id+"F1.opExtrude","SWEPT_EDGE",EDGE,{"disambiguationData":[OSD([sQuery(id+"F0.wireOp",EDGE,"E0.sketch_text.stroke-43"),sQuery(id+"F0.wireOp",EDGE,"E0.sketch_text.stroke-44")])]});
            var Q72;
            Q72=makeQuery(id+"F1.opExtrude","CAP_EDGE",EDGE,{"disambiguationData":[OSD([sQuery(id+"F0.wireOp",EDGE,"E0.sketch_text.stroke-36")])],"isStart":true});
            var Q73;
            Q73=makeQuery(id+"F1.opExtrude","CAP_EDGE",EDGE,{"disambiguationData":[OSD([sQuery(id+"F0.wireOp",EDGE,"E0.sketch_text.stroke-44")])],"isStart":true});
            fillet(context, id + "F7", {"entities" : qUnion([Q0, Q1, Q2, Q3, Q4, Q5, Q6, Q7, Q8, Q9, Q10, Q11, Q12, Q13, Q14, Q15, Q16, Q17, Q18, Q19, Q20, Q21, Q22, Q23, Q24, Q25, Q26, Q27, Q28, Q29, Q30, Q31, Q32, Q33, Q34, Q35, Q36, Q37, Q38, Q39, Q40, Q41, Q42, Q43, Q44, Q45, Q46, Q47, Q48, Q49, Q50, Q51, Q52, Q53, Q54, Q55, Q56, Q57, Q58, Q59, Q60, Q61, Q62, Q63, Q64, Q65, Q66, Q67, Q68, Q69, Q70, Q71, Q72, Q73]), "radius" : getVariable(context, 'FilletAmount'), "tangentPropagation" : true, "allowEdgeOverflow" : false});
        }
        {
            var Q0;
            Q0=makeQuery(id+"F1.opExtrude","SWEPT_FACE",FACE,{"disambiguationData":[OSD([sQuery(id+"F0.wireOp",EDGE,"E0.sketch_text.stroke-51")])]});
            var Q1;
            Q1=makeQuery(id+"F1.opExtrude","SWEPT_FACE",FACE,{"disambiguationData":[OSD([sQuery(id+"F0.wireOp",EDGE,"E0.sketch_text.stroke-67")])]});
            var Q2;
            Q2=makeQuery(id+"F1.opExtrude","CAP_EDGE",EDGE,{"disambiguationData":[OSD([sQuery(id+"F0.wireOp",EDGE,"E0.sketch_text.stroke-52")])],"isStart":false});
            var Q3;
            Q3=makeQuery(id+"F1.opExtrude","CAP_EDGE",EDGE,{"disambiguationData":[OSD([sQuery(id+"F0.wireOp",EDGE,"E0.sketch_text.stroke-60")])],"isStart":false});
            var Q4;
            Q4=makeQuery(id+"F1.opExtrude","SWEPT_FACE",FACE,{"disambiguationData":[OSD([sQuery(id+"F0.wireOp",EDGE,"E0.sketch_text.stroke-65")])]});
            var Q5;
            Q5=makeQuery(id+"F1.opExtrude","CAP_FACE",FACE,{"disambiguationData":[OSD([sQuery(id+"F0.wireOp",EDGE,"E0.sketch_text.stroke-50"),sQuery(id+"F0.wireOp",EDGE,"E0.sketch_text.stroke-51"),sQuery(id+"F0.wireOp",EDGE,"E0.sketch_text.stroke-52"),sQuery(id+"F0.wireOp",EDGE,"E0.sketch_text.stroke-53"),sQuery(id+"F0.wireOp",EDGE,"E0.sketch_text.stroke-54"),sQuery(id+"F0.wireOp",EDGE,"E0.sketch_text.stroke-55"),sQuery(id+"F0.wireOp",EDGE,"E0.sketch_text.stroke-56"),sQuery(id+"F0.wireOp",EDGE,"E0.sketch_text.stroke-57"),sQuery(id+"F0.wireOp",EDGE,"E0.sketch_text.stroke-58"),sQuery(id+"F0.wireOp",EDGE,"E0.sketch_text.stroke-59"),sQuery(id+"F0.wireOp",EDGE,"E0.sketch_text.stroke-60"),sQuery(id+"F0.wireOp",EDGE,"E0.sketch_text.stroke-61"),sQuery(id+"F0.wireOp",EDGE,"E0.sketch_text.stroke-62"),sQuery(id+"F0.wireOp",EDGE,"E0.sketch_text.stroke-63"),sQuery(id+"F0.wireOp",EDGE,"E0.sketch_text.stroke-64"),sQuery(id+"F0.wireOp",EDGE,"E0.sketch_text.stroke-65"),sQuery(id+"F0.wireOp",EDGE,"E0.sketch_text.stroke-66"),sQuery(id+"F0.wireOp",EDGE,"E0.sketch_text.stroke-67")])],"isStart":false});
            var Q6;
            Q6=makeQuery(id+"F1.opExtrude","SWEPT_FACE",FACE,{"disambiguationData":[OSD([sQuery(id+"F0.wireOp",EDGE,"E0.sketch_text.stroke-66")])]});
            var Q7;
            Q7=makeQuery(id+"F1.opExtrude","CAP_EDGE",EDGE,{"disambiguationData":[OSD([sQuery(id+"F0.wireOp",EDGE,"E0.sketch_text.stroke-53")])],"isStart":false});
            var Q8;
            Q8=makeQuery(id+"F1.opExtrude","CAP_EDGE",EDGE,{"disambiguationData":[OSD([sQuery(id+"F0.wireOp",EDGE,"E0.sketch_text.stroke-61")])],"isStart":false});
            var Q9;
            Q9=makeQuery(id+"F1.opExtrude","SWEPT_FACE",FACE,{"disambiguationData":[OSD([sQuery(id+"F0.wireOp",EDGE,"E0.sketch_text.stroke-52")])]});
            var Q10;
            Q10=makeQuery(id+"F1.opExtrude","CAP_EDGE",EDGE,{"disambiguationData":[OSD([sQuery(id+"F0.wireOp",EDGE,"E0.sketch_text.stroke-54")])],"isStart":false});
            var Q11;
            Q11=makeQuery(id+"F1.opExtrude","CAP_EDGE",EDGE,{"disambiguationData":[OSD([sQuery(id+"F0.wireOp",EDGE,"E0.sketch_text.stroke-62")])],"isStart":false});
            var Q12;
            Q12=makeQuery(id+"F1.opExtrude","SWEPT_FACE",FACE,{"disambiguationData":[OSD([sQuery(id+"F0.wireOp",EDGE,"E0.sketch_text.stroke-53")])]});
            var Q13;
            Q13=makeQuery(id+"F1.opExtrude","SWEPT_FACE",FACE,{"disambiguationData":[OSD([sQuery(id+"F0.wireOp",EDGE,"E0.sketch_text.stroke-54")])]});
            var Q14;
            Q14=makeQuery(id+"F1.opExtrude","CAP_EDGE",EDGE,{"disambiguationData":[OSD([sQuery(id+"F0.wireOp",EDGE,"E0.sketch_text.stroke-55")])],"isStart":false});
            var Q15;
            Q15=makeQuery(id+"F1.opExtrude","CAP_EDGE",EDGE,{"disambiguationData":[OSD([sQuery(id+"F0.wireOp",EDGE,"E0.sketch_text.stroke-63")])],"isStart":false});
            var Q16;
            Q16=makeQuery(id+"F1.opExtrude","SWEPT_FACE",FACE,{"disambiguationData":[OSD([sQuery(id+"F0.wireOp",EDGE,"E0.sketch_text.stroke-55")])]});
            var Q17;
            Q17=makeQuery(id+"F1.opExtrude","SWEPT_FACE",FACE,{"disambiguationData":[OSD([sQuery(id+"F0.wireOp",EDGE,"E0.sketch_text.stroke-56")])]});
            var Q18;
            Q18=makeQuery(id+"F1.opExtrude","CAP_EDGE",EDGE,{"disambiguationData":[OSD([sQuery(id+"F0.wireOp",EDGE,"E0.sketch_text.stroke-56")])],"isStart":false});
            var Q19;
            Q19=makeQuery(id+"F1.opExtrude","CAP_EDGE",EDGE,{"disambiguationData":[OSD([sQuery(id+"F0.wireOp",EDGE,"E0.sketch_text.stroke-64")])],"isStart":false});
            var Q20;
            Q20=makeQuery(id+"F1.opExtrude","SWEPT_FACE",FACE,{"disambiguationData":[OSD([sQuery(id+"F0.wireOp",EDGE,"E0.sketch_text.stroke-57")])]});
            var Q21;
            Q21=makeQuery(id+"F1.opExtrude","SWEPT_FACE",FACE,{"disambiguationData":[OSD([sQuery(id+"F0.wireOp",EDGE,"E0.sketch_text.stroke-58")])]});
            var Q22;
            Q22=makeQuery(id+"F1.opExtrude","CAP_EDGE",EDGE,{"disambiguationData":[OSD([sQuery(id+"F0.wireOp",EDGE,"E0.sketch_text.stroke-57")])],"isStart":false});
            var Q23;
            Q23=makeQuery(id+"F1.opExtrude","CAP_EDGE",EDGE,{"disambiguationData":[OSD([sQuery(id+"F0.wireOp",EDGE,"E0.sketch_text.stroke-65")])],"isStart":false});
            var Q24;
            Q24=makeQuery(id+"F1.opExtrude","SWEPT_FACE",FACE,{"disambiguationData":[OSD([sQuery(id+"F0.wireOp",EDGE,"E0.sketch_text.stroke-59")])]});
            var Q25;
            Q25=makeQuery(id+"F1.opExtrude","SWEPT_FACE",FACE,{"disambiguationData":[OSD([sQuery(id+"F0.wireOp",EDGE,"E0.sketch_text.stroke-60")])]});
            var Q26;
            Q26=makeQuery(id+"F1.opExtrude","CAP_EDGE",EDGE,{"disambiguationData":[OSD([sQuery(id+"F0.wireOp",EDGE,"E0.sketch_text.stroke-50")])],"isStart":false});
            var Q27;
            Q27=makeQuery(id+"F1.opExtrude","CAP_EDGE",EDGE,{"disambiguationData":[OSD([sQuery(id+"F0.wireOp",EDGE,"E0.sketch_text.stroke-58")])],"isStart":false});
            var Q28;
            Q28=makeQuery(id+"F1.opExtrude","CAP_EDGE",EDGE,{"disambiguationData":[OSD([sQuery(id+"F0.wireOp",EDGE,"E0.sketch_text.stroke-66")])],"isStart":false});
            var Q29;
            Q29=makeQuery(id+"F1.opExtrude","SWEPT_FACE",FACE,{"disambiguationData":[OSD([sQuery(id+"F0.wireOp",EDGE,"E0.sketch_text.stroke-61")])]});
            var Q30;
            Q30=makeQuery(id+"F1.opExtrude","SWEPT_FACE",FACE,{"disambiguationData":[OSD([sQuery(id+"F0.wireOp",EDGE,"E0.sketch_text.stroke-62")])]});
            var Q31;
            Q31=makeQuery(id+"F1.opExtrude","CAP_EDGE",EDGE,{"disambiguationData":[OSD([sQuery(id+"F0.wireOp",EDGE,"E0.sketch_text.stroke-51")])],"isStart":false});
            var Q32;
            Q32=makeQuery(id+"F1.opExtrude","CAP_EDGE",EDGE,{"disambiguationData":[OSD([sQuery(id+"F0.wireOp",EDGE,"E0.sketch_text.stroke-59")])],"isStart":false});
            var Q33;
            Q33=makeQuery(id+"F1.opExtrude","CAP_EDGE",EDGE,{"disambiguationData":[OSD([sQuery(id+"F0.wireOp",EDGE,"E0.sketch_text.stroke-67")])],"isStart":false});
            var Q34;
            Q34=makeQuery(id+"F1.opExtrude","SWEPT_FACE",FACE,{"disambiguationData":[OSD([sQuery(id+"F0.wireOp",EDGE,"E0.sketch_text.stroke-63")])]});
            var Q35;
            Q35=makeQuery(id+"F1.opExtrude","SWEPT_FACE",FACE,{"disambiguationData":[OSD([sQuery(id+"F0.wireOp",EDGE,"E0.sketch_text.stroke-50")])]});
            var Q36;
            Q36=makeQuery(id+"F1.opExtrude","SWEPT_FACE",FACE,{"disambiguationData":[OSD([sQuery(id+"F0.wireOp",EDGE,"E0.sketch_text.stroke-64")])]});
            var Q37;
            Q37=makeQuery(id+"F1.opExtrude","SWEPT_EDGE",EDGE,{"disambiguationData":[OSD([sQuery(id+"F0.wireOp",EDGE,"E0.sketch_text.stroke-60"),sQuery(id+"F0.wireOp",EDGE,"E0.sketch_text.stroke-61")])]});
            var Q38;
            Q38=makeQuery(id+"F1.opExtrude","CAP_FACE",FACE,{"disambiguationData":[OSD([sQuery(id+"F0.wireOp",EDGE,"E0.sketch_text.stroke-50"),sQuery(id+"F0.wireOp",EDGE,"E0.sketch_text.stroke-51"),sQuery(id+"F0.wireOp",EDGE,"E0.sketch_text.stroke-52"),sQuery(id+"F0.wireOp",EDGE,"E0.sketch_text.stroke-53"),sQuery(id+"F0.wireOp",EDGE,"E0.sketch_text.stroke-54"),sQuery(id+"F0.wireOp",EDGE,"E0.sketch_text.stroke-55"),sQuery(id+"F0.wireOp",EDGE,"E0.sketch_text.stroke-56"),sQuery(id+"F0.wireOp",EDGE,"E0.sketch_text.stroke-57"),sQuery(id+"F0.wireOp",EDGE,"E0.sketch_text.stroke-58"),sQuery(id+"F0.wireOp",EDGE,"E0.sketch_text.stroke-59"),sQuery(id+"F0.wireOp",EDGE,"E0.sketch_text.stroke-60"),sQuery(id+"F0.wireOp",EDGE,"E0.sketch_text.stroke-61"),sQuery(id+"F0.wireOp",EDGE,"E0.sketch_text.stroke-62"),sQuery(id+"F0.wireOp",EDGE,"E0.sketch_text.stroke-63"),sQuery(id+"F0.wireOp",EDGE,"E0.sketch_text.stroke-64"),sQuery(id+"F0.wireOp",EDGE,"E0.sketch_text.stroke-65"),sQuery(id+"F0.wireOp",EDGE,"E0.sketch_text.stroke-66"),sQuery(id+"F0.wireOp",EDGE,"E0.sketch_text.stroke-67")])],"isStart":true});
            var Q39;
            Q39=makeQuery(id+"F1.opExtrude","SWEPT_EDGE",EDGE,{"disambiguationData":[OSD([sQuery(id+"F0.wireOp",EDGE,"E0.sketch_text.stroke-61"),sQuery(id+"F0.wireOp",EDGE,"E0.sketch_text.stroke-62")])]});
            var Q40;
            Q40=makeQuery(id+"F1.opExtrude","CAP_EDGE",EDGE,{"disambiguationData":[OSD([sQuery(id+"F0.wireOp",EDGE,"E0.sketch_text.stroke-53")])],"isStart":true});
            var Q41;
            Q41=makeQuery(id+"F1.opExtrude","CAP_EDGE",EDGE,{"disambiguationData":[OSD([sQuery(id+"F0.wireOp",EDGE,"E0.sketch_text.stroke-61")])],"isStart":true});
            var Q42;
            Q42=makeQuery(id+"F1.opExtrude","SWEPT_EDGE",EDGE,{"disambiguationData":[OSD([sQuery(id+"F0.wireOp",EDGE,"E0.sketch_text.stroke-62"),sQuery(id+"F0.wireOp",EDGE,"E0.sketch_text.stroke-63")])]});
            var Q43;
            Q43=makeQuery(id+"F1.opExtrude","SWEPT_EDGE",EDGE,{"disambiguationData":[OSD([sQuery(id+"F0.wireOp",EDGE,"E0.sketch_text.stroke-63"),sQuery(id+"F0.wireOp",EDGE,"E0.sketch_text.stroke-64")])]});
            var Q44;
            Q44=makeQuery(id+"F1.opExtrude","CAP_EDGE",EDGE,{"disambiguationData":[OSD([sQuery(id+"F0.wireOp",EDGE,"E0.sketch_text.stroke-54")])],"isStart":true});
            var Q45;
            Q45=makeQuery(id+"F1.opExtrude","CAP_EDGE",EDGE,{"disambiguationData":[OSD([sQuery(id+"F0.wireOp",EDGE,"E0.sketch_text.stroke-62")])],"isStart":true});
            var Q46;
            Q46=makeQuery(id+"F1.opExtrude","SWEPT_EDGE",EDGE,{"disambiguationData":[OSD([sQuery(id+"F0.wireOp",EDGE,"E0.sketch_text.stroke-64"),sQuery(id+"F0.wireOp",EDGE,"E0.sketch_text.stroke-65")])]});
            var Q47;
            Q47=makeQuery(id+"F1.opExtrude","SWEPT_EDGE",EDGE,{"disambiguationData":[OSD([sQuery(id+"F0.wireOp",EDGE,"E0.sketch_text.stroke-50"),sQuery(id+"F0.wireOp",EDGE,"E0.sketch_text.stroke-57")])]});
            var Q48;
            Q48=makeQuery(id+"F1.opExtrude","SWEPT_EDGE",EDGE,{"disambiguationData":[OSD([sQuery(id+"F0.wireOp",EDGE,"E0.sketch_text.stroke-65"),sQuery(id+"F0.wireOp",EDGE,"E0.sketch_text.stroke-66")])]});
            var Q49;
            Q49=makeQuery(id+"F1.opExtrude","CAP_EDGE",EDGE,{"disambiguationData":[OSD([sQuery(id+"F0.wireOp",EDGE,"E0.sketch_text.stroke-55")])],"isStart":true});
            var Q50;
            Q50=makeQuery(id+"F1.opExtrude","CAP_EDGE",EDGE,{"disambiguationData":[OSD([sQuery(id+"F0.wireOp",EDGE,"E0.sketch_text.stroke-63")])],"isStart":true});
            var Q51;
            Q51=makeQuery(id+"F1.opExtrude","SWEPT_EDGE",EDGE,{"disambiguationData":[OSD([sQuery(id+"F0.wireOp",EDGE,"E0.sketch_text.stroke-50"),sQuery(id+"F0.wireOp",EDGE,"E0.sketch_text.stroke-51")])]});
            var Q52;
            Q52=makeQuery(id+"F1.opExtrude","SWEPT_EDGE",EDGE,{"disambiguationData":[OSD([sQuery(id+"F0.wireOp",EDGE,"E0.sketch_text.stroke-66"),sQuery(id+"F0.wireOp",EDGE,"E0.sketch_text.stroke-67")])]});
            var Q53;
            Q53=makeQuery(id+"F1.opExtrude","SWEPT_EDGE",EDGE,{"disambiguationData":[OSD([sQuery(id+"F0.wireOp",EDGE,"E0.sketch_text.stroke-51"),sQuery(id+"F0.wireOp",EDGE,"E0.sketch_text.stroke-52")])]});
            var Q54;
            Q54=makeQuery(id+"F1.opExtrude","CAP_EDGE",EDGE,{"disambiguationData":[OSD([sQuery(id+"F0.wireOp",EDGE,"E0.sketch_text.stroke-56")])],"isStart":true});
            var Q55;
            Q55=makeQuery(id+"F1.opExtrude","CAP_EDGE",EDGE,{"disambiguationData":[OSD([sQuery(id+"F0.wireOp",EDGE,"E0.sketch_text.stroke-64")])],"isStart":true});
            var Q56;
            Q56=makeQuery(id+"F1.opExtrude","SWEPT_EDGE",EDGE,{"disambiguationData":[OSD([sQuery(id+"F0.wireOp",EDGE,"E0.sketch_text.stroke-52"),sQuery(id+"F0.wireOp",EDGE,"E0.sketch_text.stroke-53")])]});
            var Q57;
            Q57=makeQuery(id+"F1.opExtrude","SWEPT_EDGE",EDGE,{"disambiguationData":[OSD([sQuery(id+"F0.wireOp",EDGE,"E0.sketch_text.stroke-53"),sQuery(id+"F0.wireOp",EDGE,"E0.sketch_text.stroke-54")])]});
            var Q58;
            Q58=makeQuery(id+"F1.opExtrude","CAP_EDGE",EDGE,{"disambiguationData":[OSD([sQuery(id+"F0.wireOp",EDGE,"E0.sketch_text.stroke-57")])],"isStart":true});
            var Q59;
            Q59=makeQuery(id+"F1.opExtrude","CAP_EDGE",EDGE,{"disambiguationData":[OSD([sQuery(id+"F0.wireOp",EDGE,"E0.sketch_text.stroke-65")])],"isStart":true});
            var Q60;
            Q60=makeQuery(id+"F1.opExtrude","SWEPT_EDGE",EDGE,{"disambiguationData":[OSD([sQuery(id+"F0.wireOp",EDGE,"E0.sketch_text.stroke-54"),sQuery(id+"F0.wireOp",EDGE,"E0.sketch_text.stroke-55")])]});
            var Q61;
            Q61=makeQuery(id+"F1.opExtrude","SWEPT_EDGE",EDGE,{"disambiguationData":[OSD([sQuery(id+"F0.wireOp",EDGE,"E0.sketch_text.stroke-55"),sQuery(id+"F0.wireOp",EDGE,"E0.sketch_text.stroke-56")])]});
            var Q62;
            Q62=makeQuery(id+"F1.opExtrude","CAP_EDGE",EDGE,{"disambiguationData":[OSD([sQuery(id+"F0.wireOp",EDGE,"E0.sketch_text.stroke-50")])],"isStart":true});
            var Q63;
            Q63=makeQuery(id+"F1.opExtrude","CAP_EDGE",EDGE,{"disambiguationData":[OSD([sQuery(id+"F0.wireOp",EDGE,"E0.sketch_text.stroke-58")])],"isStart":true});
            var Q64;
            Q64=makeQuery(id+"F1.opExtrude","CAP_EDGE",EDGE,{"disambiguationData":[OSD([sQuery(id+"F0.wireOp",EDGE,"E0.sketch_text.stroke-66")])],"isStart":true});
            var Q65;
            Q65=makeQuery(id+"F1.opExtrude","SWEPT_EDGE",EDGE,{"disambiguationData":[OSD([sQuery(id+"F0.wireOp",EDGE,"E0.sketch_text.stroke-56"),sQuery(id+"F0.wireOp",EDGE,"E0.sketch_text.stroke-57")])]});
            var Q66;
            Q66=makeQuery(id+"F1.opExtrude","SWEPT_EDGE",EDGE,{"disambiguationData":[OSD([sQuery(id+"F0.wireOp",EDGE,"E0.sketch_text.stroke-58"),sQuery(id+"F0.wireOp",EDGE,"E0.sketch_text.stroke-67")])]});
            var Q67;
            Q67=makeQuery(id+"F1.opExtrude","CAP_EDGE",EDGE,{"disambiguationData":[OSD([sQuery(id+"F0.wireOp",EDGE,"E0.sketch_text.stroke-51")])],"isStart":true});
            var Q68;
            Q68=makeQuery(id+"F1.opExtrude","CAP_EDGE",EDGE,{"disambiguationData":[OSD([sQuery(id+"F0.wireOp",EDGE,"E0.sketch_text.stroke-59")])],"isStart":true});
            var Q69;
            Q69=makeQuery(id+"F1.opExtrude","CAP_EDGE",EDGE,{"disambiguationData":[OSD([sQuery(id+"F0.wireOp",EDGE,"E0.sketch_text.stroke-67")])],"isStart":true});
            var Q70;
            Q70=makeQuery(id+"F1.opExtrude","SWEPT_EDGE",EDGE,{"disambiguationData":[OSD([sQuery(id+"F0.wireOp",EDGE,"E0.sketch_text.stroke-58"),sQuery(id+"F0.wireOp",EDGE,"E0.sketch_text.stroke-59")])]});
            var Q71;
            Q71=makeQuery(id+"F1.opExtrude","SWEPT_EDGE",EDGE,{"disambiguationData":[OSD([sQuery(id+"F0.wireOp",EDGE,"E0.sketch_text.stroke-59"),sQuery(id+"F0.wireOp",EDGE,"E0.sketch_text.stroke-60")])]});
            var Q72;
            Q72=makeQuery(id+"F1.opExtrude","CAP_EDGE",EDGE,{"disambiguationData":[OSD([sQuery(id+"F0.wireOp",EDGE,"E0.sketch_text.stroke-52")])],"isStart":true});
            var Q73;
            Q73=makeQuery(id+"F1.opExtrude","CAP_EDGE",EDGE,{"disambiguationData":[OSD([sQuery(id+"F0.wireOp",EDGE,"E0.sketch_text.stroke-60")])],"isStart":true});
            fillet(context, id + "F8", {"entities" : qUnion([Q0, Q1, Q2, Q3, Q4, Q5, Q6, Q7, Q8, Q9, Q10, Q11, Q12, Q13, Q14, Q15, Q16, Q17, Q18, Q19, Q20, Q21, Q22, Q23, Q24, Q25, Q26, Q27, Q28, Q29, Q30, Q31, Q32, Q33, Q34, Q35, Q36, Q37, Q38, Q39, Q40, Q41, Q42, Q43, Q44, Q45, Q46, Q47, Q48, Q49, Q50, Q51, Q52, Q53, Q54, Q55, Q56, Q57, Q58, Q59, Q60, Q61, Q62, Q63, Q64, Q65, Q66, Q67, Q68, Q69, Q70, Q71, Q72, Q73]), "radius" : getVariable(context, 'FilletAmount'), "tangentPropagation" : true, "allowEdgeOverflow" : false});
        }
        {
            var Q0;
            Q0=makeQuery(id+"F1.opExtrude","CAP_FACE",FACE,{"disambiguationData":[OSD([sQuery(id+"F0.wireOp",EDGE,"E0.sketch_text.stroke-9"),sQuery(id+"F0.wireOp",EDGE,"E0.sketch_text.stroke-10"),sQuery(id+"F0.wireOp",EDGE,"E0.sketch_text.stroke-11"),sQuery(id+"F0.wireOp",EDGE,"E0.sketch_text.stroke-12"),sQuery(id+"F0.wireOp",EDGE,"E0.sketch_text.stroke-13"),sQuery(id+"F0.wireOp",EDGE,"E0.sketch_text.stroke-14"),sQuery(id+"F0.wireOp",EDGE,"E0.sketch_text.stroke-15"),sQuery(id+"F0.wireOp",EDGE,"E0.sketch_text.stroke-16"),sQuery(id+"F0.wireOp",EDGE,"E0.sketch_text.stroke-17"),sQuery(id+"F0.wireOp",EDGE,"E0.sketch_text.stroke-18"),sQuery(id+"F0.wireOp",EDGE,"E0.sketch_text.stroke-19"),sQuery(id+"F0.wireOp",EDGE,"E0.sketch_text.stroke-20"),sQuery(id+"F0.wireOp",EDGE,"E0.sketch_text.stroke-21"),sQuery(id+"F0.wireOp",EDGE,"E0.sketch_text.stroke-22"),sQuery(id+"F0.wireOp",EDGE,"E0.sketch_text.stroke-23"),sQuery(id+"F0.wireOp",EDGE,"E0.sketch_text.stroke-24"),sQuery(id+"F0.wireOp",EDGE,"E0.sketch_text.stroke-25"),sQuery(id+"F0.wireOp",EDGE,"E0.sketch_text.stroke-26"),sQuery(id+"F0.wireOp",EDGE,"E0.sketch_text.stroke-27")])],"isStart":false});
            var Q1;
            Q1=makeQuery(id+"F1.opExtrude","CAP_FACE",FACE,{"disambiguationData":[OSD([sQuery(id+"F0.wireOp",EDGE,"E0.sketch_text.stroke-0"),sQuery(id+"F0.wireOp",EDGE,"E0.sketch_text.stroke-1"),sQuery(id+"F0.wireOp",EDGE,"E0.sketch_text.stroke-2"),sQuery(id+"F0.wireOp",EDGE,"E0.sketch_text.stroke-3"),sQuery(id+"F0.wireOp",EDGE,"E0.sketch_text.stroke-4")])],"isStart":false});
            var Q2;
            Q2=makeQuery(id+"F1.opExtrude","CAP_FACE",FACE,{"disambiguationData":[OSD([sQuery(id+"F0.wireOp",EDGE,"E0.sketch_text.stroke-28"),sQuery(id+"F0.wireOp",EDGE,"E0.sketch_text.stroke-29"),sQuery(id+"F0.wireOp",EDGE,"E0.sketch_text.stroke-30"),sQuery(id+"F0.wireOp",EDGE,"E0.sketch_text.stroke-31")])],"isStart":false});
            var Q3;
            Q3=makeQuery(id+"F1.opExtrude","CAP_FACE",FACE,{"disambiguationData":[OSD([sQuery(id+"F0.wireOp",EDGE,"E0.sketch_text.stroke-32"),sQuery(id+"F0.wireOp",EDGE,"E0.sketch_text.stroke-33"),sQuery(id+"F0.wireOp",EDGE,"E0.sketch_text.stroke-34"),sQuery(id+"F0.wireOp",EDGE,"E0.sketch_text.stroke-35"),sQuery(id+"F0.wireOp",EDGE,"E0.sketch_text.stroke-36"),sQuery(id+"F0.wireOp",EDGE,"E0.sketch_text.stroke-37"),sQuery(id+"F0.wireOp",EDGE,"E0.sketch_text.stroke-38"),sQuery(id+"F0.wireOp",EDGE,"E0.sketch_text.stroke-39"),sQuery(id+"F0.wireOp",EDGE,"E0.sketch_text.stroke-40"),sQuery(id+"F0.wireOp",EDGE,"E0.sketch_text.stroke-41"),sQuery(id+"F0.wireOp",EDGE,"E0.sketch_text.stroke-42"),sQuery(id+"F0.wireOp",EDGE,"E0.sketch_text.stroke-43"),sQuery(id+"F0.wireOp",EDGE,"E0.sketch_text.stroke-44"),sQuery(id+"F0.wireOp",EDGE,"E0.sketch_text.stroke-45"),sQuery(id+"F0.wireOp",EDGE,"E0.sketch_text.stroke-46"),sQuery(id+"F0.wireOp",EDGE,"E0.sketch_text.stroke-47"),sQuery(id+"F0.wireOp",EDGE,"E0.sketch_text.stroke-48"),sQuery(id+"F0.wireOp",EDGE,"E0.sketch_text.stroke-49")])],"isStart":false});
            var Q4;
            Q4=makeQuery(id+"F1.opExtrude","CAP_FACE",FACE,{"disambiguationData":[OSD([sQuery(id+"F0.wireOp",EDGE,"E0.sketch_text.stroke-50"),sQuery(id+"F0.wireOp",EDGE,"E0.sketch_text.stroke-51"),sQuery(id+"F0.wireOp",EDGE,"E0.sketch_text.stroke-52"),sQuery(id+"F0.wireOp",EDGE,"E0.sketch_text.stroke-53"),sQuery(id+"F0.wireOp",EDGE,"E0.sketch_text.stroke-54"),sQuery(id+"F0.wireOp",EDGE,"E0.sketch_text.stroke-55"),sQuery(id+"F0.wireOp",EDGE,"E0.sketch_text.stroke-56"),sQuery(id+"F0.wireOp",EDGE,"E0.sketch_text.stroke-57"),sQuery(id+"F0.wireOp",EDGE,"E0.sketch_text.stroke-58"),sQuery(id+"F0.wireOp",EDGE,"E0.sketch_text.stroke-59"),sQuery(id+"F0.wireOp",EDGE,"E0.sketch_text.stroke-60"),sQuery(id+"F0.wireOp",EDGE,"E0.sketch_text.stroke-61"),sQuery(id+"F0.wireOp",EDGE,"E0.sketch_text.stroke-62"),sQuery(id+"F0.wireOp",EDGE,"E0.sketch_text.stroke-63"),sQuery(id+"F0.wireOp",EDGE,"E0.sketch_text.stroke-64"),sQuery(id+"F0.wireOp",EDGE,"E0.sketch_text.stroke-65"),sQuery(id+"F0.wireOp",EDGE,"E0.sketch_text.stroke-66"),sQuery(id+"F0.wireOp",EDGE,"E0.sketch_text.stroke-67")])],"isStart":false});
            var Q5;
            Q5=makeQuery(id+"F1.opExtrude","CAP_FACE",FACE,{"disambiguationData":[OSD([sQuery(id+"F0.wireOp",EDGE,"E0.sketch_text.stroke-5"),sQuery(id+"F0.wireOp",EDGE,"E0.sketch_text.stroke-6"),sQuery(id+"F0.wireOp",EDGE,"E0.sketch_text.stroke-7"),sQuery(id+"F0.wireOp",EDGE,"E0.sketch_text.stroke-8")])],"isStart":false});
            shell(context, id + "F9", {"entities" : qUnion([Q0, Q1, Q2, Q3, Q4, Q5]), "thickness" : 2.54 * mm});
        }
    });
